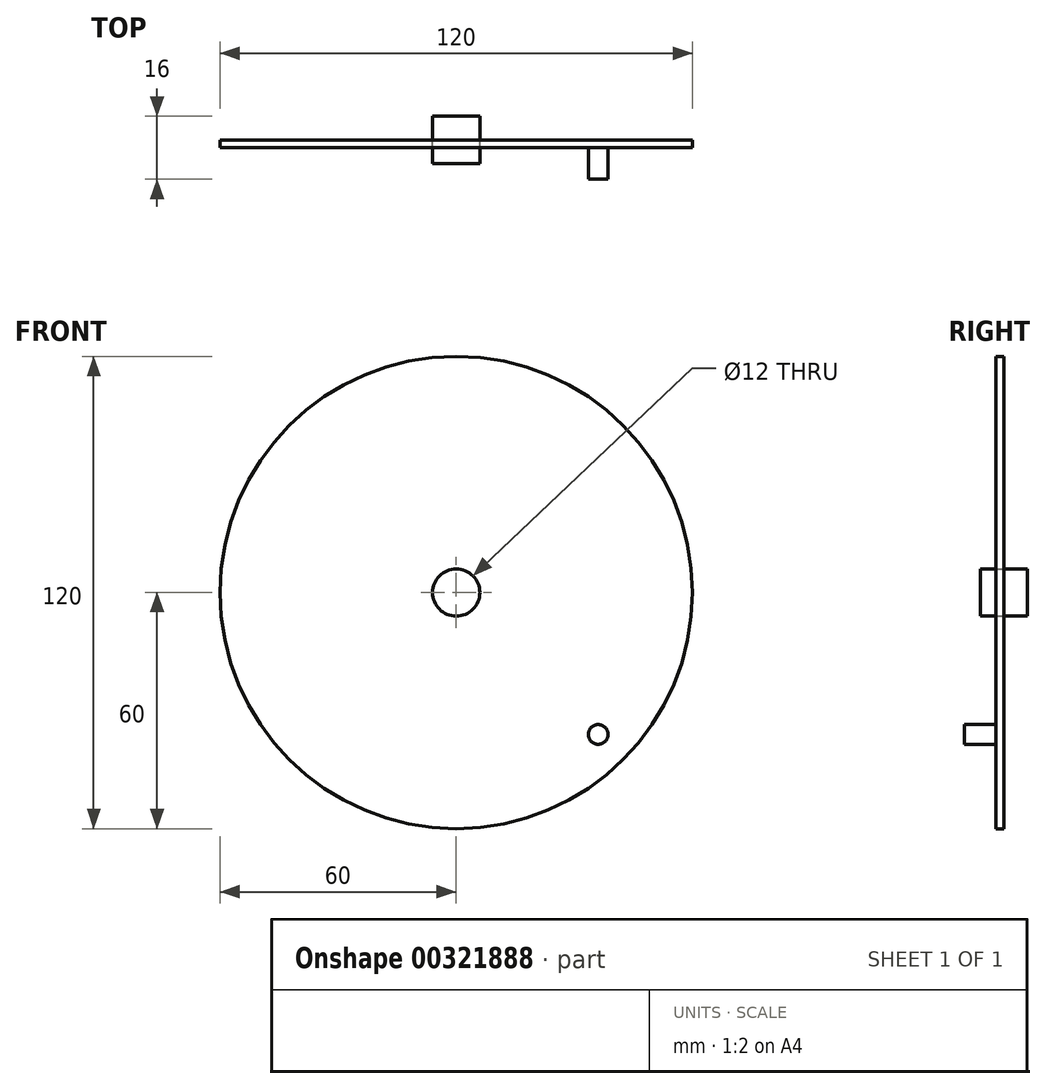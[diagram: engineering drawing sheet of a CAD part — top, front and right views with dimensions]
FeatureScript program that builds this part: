
annotation { "Feature Type Name" : "Feature", "Feature Type Description" : "" }
export const myFeature = defineFeature(function(context is Context, id is Id, definition is map)
    precondition{}
    {
        {
            var Q0;
            Q0=qCreatedBy(makeId("Front.planeOp"),FACE);
            var sketch = newSketch(context, id + "F0", { "sketchPlane" : qUnion([Q0])});
            skCircle(sketch, "E0", {"center": v(0, 0) * mm, "radius": 60 * mm});
            skCircle(sketch, "E1", {"center": v(0, 0) * mm, "radius": 6 * mm});
            skSolve(sketch);
        }
        {
            var Q0;
            Q0=makeQuery(id+"F0.imprint","IMPRINT",FACE,{"disambiguationData":[TD([[makeQuery(id+"F0.imprint","IMPRINT",EDGE,{"derivedFrom":sQuery(id+"F0.wireOp",EDGE,"E0")}),1.0]])]});
            extrude(context, id + "F1", {"entities" : qUnion([Q0]), "depth" : 2 * mm});
        }
        {
            var Q0;
            Q0=makeQuery(id+"F0.imprint","IMPRINT",FACE,{"disambiguationData":[TD([[makeQuery(id+"F0.imprint","IMPRINT",EDGE,{"derivedFrom":sQuery(id+"F0.wireOp",EDGE,"E1")}),1.0]])]});
            extrude(context, id + "F2", {"entities" : qUnion([Q0]), "endBound" : BoundingType.SYMMETRIC, "depth" : 12 * mm});
        }
        {
            var Q0;
            Q0=makeQuery(id+"F1.opExtrude","CAP_FACE",FACE,{"disambiguationData":[OSD([sQuery(id+"F0.wireOp",EDGE,"E0"),sQuery(id+"F0.wireOp",EDGE,"E1")])],"isStart":false});
            var sketch = newSketch(context, id + "F3", { "sketchPlane" : qUnion([Q0])});
            skLineSegment(sketch, "E2", {"start": v(0, 0) * mm, "end": v(112.68, -112.68) * mm, "construction": true});
            skPoint(sketch, "E3", {"position": v(32, -32) * mm});
            skPoint(sketch, "E4", {"position": v(36.06, -36.06) * mm});
            skCircle(sketch, "E5", {"center": v(36.06, -36.06) * mm, "radius": 2.5 * mm});
            skSolve(sketch);
        }
        {
            var Q0;
            Q0 = qSketchRegion(id + "F3", true);
            extrude(context, id + "F4", {"entities" : qUnion([Q0]), "operationType" : NewBodyOperationType.ADD, "depth" : 8 * mm});
        }
    });
